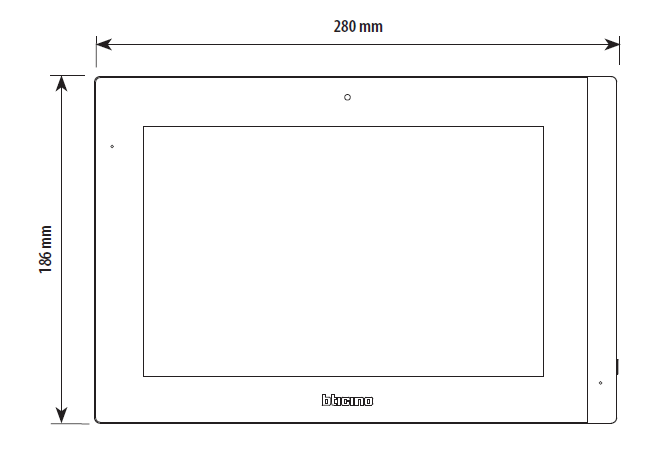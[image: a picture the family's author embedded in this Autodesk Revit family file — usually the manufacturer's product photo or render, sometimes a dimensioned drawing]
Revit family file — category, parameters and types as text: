
# Revit family: Bticino-Portier-IP-Poste Intérieur Premium
name_source: partatom
category: Equipement électrique
units: mm (PartAtom-declared; Revit-internal decimal feet)

## family parameters
Configuration du panneau = Deux colonnes, circuits au sein
Cote de connecteur circulaire = Utiliser le diamètre
Couper avec des vides une fois chargée = Non
Hôte = Face
Partagée = Non
Point de calcul de pièce = Non
Type d'élément = Tableau de raccordement

## types (4) — shared parameters
Bouton ouverture porte = Oui
Conditions Générale d'Utilisation = https://export.legrand.com
Couleur = Argent
Ecran Tactile = Oui
Elévation par défaut = 1219 mm
Fabricant = BTICINO
Mode de pose = mur creux
Objet Connecté = Oui
Profondeur = 28 mm  [stored 0.0918635 ft]
Site web configurateur = https://www.homesystems-legrandgroup.com
Température d'utilisation MIN-MAX = -10/+55 °C
Tension = 24 V DC
Type d'interface = Câble RJ45
Type de raccordement = technique de réseau

## per-type parameters (varying)
| type | Avec video | Camera | Compatible avec appareil de correction auditive | Désignation produit | Hauteur | IP | L | L1 | L3 | Largeur | Référence / Modèle | Taille de l'écran (Pouces) | Visibilité cam | l1 | l2 |
| POSTE INTERIEUR 10" AVEC CAMERA | Oui | Avec Caméra | Non | IP - POSTE INTERIEUR AVEC CAMERA 10" | 186 mm  [stored 0.610236 ft] |  | 214 mm  [stored 0.7021 ft] | 28 mm  [stored 0.0918635 ft] | 16 mm  [stored 0.0524934 ft] | 280 mm  [stored 0.918635 ft] | BT-373001 | 10 | Oui | 25 mm  [stored 0.082021 ft] | 27 mm  [stored 0.0885827 ft] |
| POSTE INTERIEUR 10" | Non | Sans caméra | Non | IP - POSTE INTERIEUR 10" | 186 mm  [stored 0.610236 ft] | 30 | 214 mm  [stored 0.7021 ft] | 28 mm  [stored 0.0918635 ft] | 16 mm  [stored 0.0524934 ft] | 280 mm  [stored 0.918635 ft] | BT-373003 | 10 | Non | 25 mm  [stored 0.082021 ft] | 27 mm  [stored 0.0885827 ft] |
| POSTE INTERIEUR 7" AVEC CAMERA | Oui | Avec Caméra | Non | IP - POSTE INTERIEUR AVEC CAMERA 7" | 134 mm  [stored 0.439633 ft] | 30 | 155 mm  [stored 0.50853 ft] | 21 mm | 15 mm  [stored 0.0492126 ft] | 211 mm  [stored 0.692257 ft] | BT-373002 | 7 | Oui | 24 mm  [stored 0.0787402 ft] | 24 mm  [stored 0.0787402 ft] |
| POSTE INTERIEUR 7" | Non | Sans caméra | Oui | IP - POSTE INTERIEUR 7" | 134 mm  [stored 0.439633 ft] | 30 | 155 mm  [stored 0.50853 ft] | 21 mm | 15 mm  [stored 0.0492126 ft] | 211 mm  [stored 0.692257 ft] | BT-373004 | 7 | Non | 24 mm  [stored 0.0787402 ft] | 24 mm  [stored 0.0787402 ft] |

note: [stored X ft] marks values corroborated as IEEE doubles in the binary element streams (Revit-internal decimal feet)
